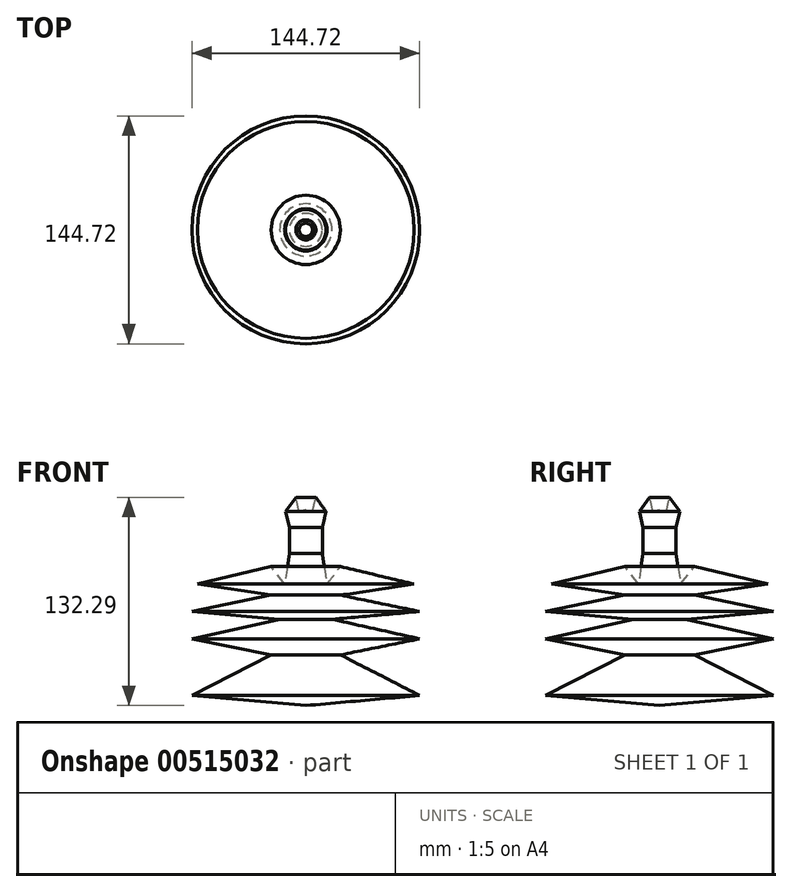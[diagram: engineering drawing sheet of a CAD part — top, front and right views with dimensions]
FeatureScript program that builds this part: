
annotation { "Feature Type Name" : "Feature", "Feature Type Description" : "" }
export const myFeature = defineFeature(function(context is Context, id is Id, definition is map)
    precondition{}
    {
        {
            var Q0;
            Q0=qCreatedBy(makeId("Front.planeOp"),FACE);
            var sketch = newSketch(context, id + "F0", { "sketchPlane" : qUnion([Q0])});
            skLineSegment(sketch, "E0", {"start": v(0, -66.94) * mm, "end": v(72.36, -60.57) * mm});
            skLineSegment(sketch, "E1", {"start": v(72.36, -60.57) * mm, "end": v(22, -34.75) * mm});
            skLineSegment(sketch, "E2", {"start": v(22, -34.75) * mm, "end": v(72.36, -24.54) * mm});
            skLineSegment(sketch, "E3", {"start": v(72.36, -24.54) * mm, "end": v(16.58, -12.11) * mm});
            skLineSegment(sketch, "E4", {"start": v(16.58, -12.11) * mm, "end": v(72.36, -7.2) * mm});
            skLineSegment(sketch, "E5", {"start": v(72.36, -7.2) * mm, "end": v(22, 3.19) * mm});
            skLineSegment(sketch, "E6", {"start": v(22, 3.19) * mm, "end": v(68.85, 10.2) * mm});
            skLineSegment(sketch, "E7", {"start": v(68.85, 10.2) * mm, "end": v(22, 21.36) * mm});
            skLineSegment(sketch, "E8", {"start": v(22, 21.36) * mm, "end": v(13.39, 10.2) * mm});
            skLineSegment(sketch, "E9", {"start": v(13.39, 10.2) * mm, "end": v(10.48, 29.6) * mm});
            skLineSegment(sketch, "E10", {"start": v(10.48, 29.6) * mm, "end": v(10.48, 46.22) * mm});
            skLineSegment(sketch, "E11", {"start": v(10.48, 46.22) * mm, "end": v(12.86, 56.21) * mm});
            skLineSegment(sketch, "E12", {"start": v(12.86, 56.21) * mm, "end": v(6.38, 65.35) * mm});
            skLineSegment(sketch, "E13", {"start": v(6.38, 65.35) * mm, "end": v(4.2, 56.21) * mm});
            skLineSegment(sketch, "E14", {"start": v(4.2, 56.21) * mm, "end": v(0, 57.21) * mm});
            skLineSegment(sketch, "E15", {"start": v(0, 57.21) * mm, "end": v(0, -66.94) * mm});
            skSolve(sketch);
        }
        {
            var Q0;
            Q0=makeQuery(id+"F0.imprint","IMPRINT",FACE,{"disambiguationData":[TD([[makeQuery(id+"F0.imprint","IMPRINT",EDGE,{"derivedFrom":sQuery(id+"F0.wireOp",EDGE,"E0")}),1.0]])]});
            var Q1;
            Q1=sQuery(id+"F0.wireOp",EDGE,"E15");
            revolve(context, id + "F1", {"entities" : qUnion([Q0]), "axis" : qUnion([Q1]), "revolveType" : RevolveType.FULL});
        }
    });
